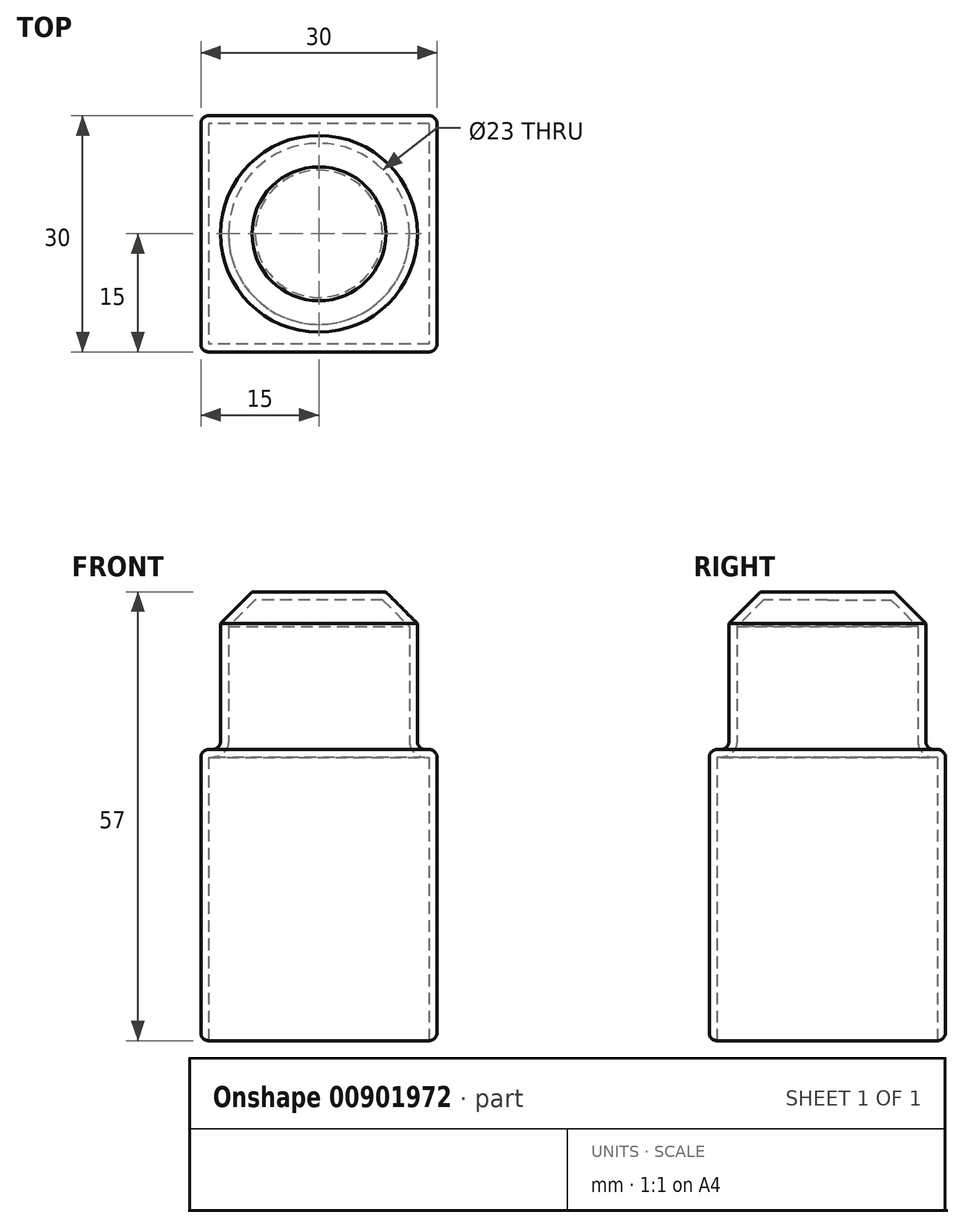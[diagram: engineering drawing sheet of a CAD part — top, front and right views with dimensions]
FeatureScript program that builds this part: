
annotation { "Feature Type Name" : "Feature", "Feature Type Description" : "" }
export const myFeature = defineFeature(function(context is Context, id is Id, definition is map)
    precondition{}
    {
        {
            var Q0;
            Q0=qCreatedBy(makeId("Top.planeOp"),FACE);
            var sketch = newSketch(context, id + "F0", { "sketchPlane" : qUnion([Q0])});
            skLineSegment(sketch, "E0.bottom", {"start": v(15, 15) * mm, "end": v(-15, 15) * mm});
            skLineSegment(sketch, "E0.top", {"start": v(15, -15) * mm, "end": v(-15, -15) * mm});
            skLineSegment(sketch, "E0.left", {"start": v(15, 15) * mm, "end": v(15, -15) * mm});
            skLineSegment(sketch, "E0.right", {"start": v(-15, 15) * mm, "end": v(-15, -15) * mm});
            skPoint(sketch, "E0.middle", {"position": v(0, 0) * mm});
            skSolve(sketch);
        }
        {
            var Q0;
            Q0 = qSketchRegion(id + "F0", true);
            extrude(context, id + "F1", {"entities" : qUnion([Q0]), "depth" : 37 * mm, "offsetDistance" : 25 * mm});
        }
        {
            var Q0;
            Q0=makeQuery(id+"F1.opExtrude","CAP_FACE",FACE,{"disambiguationData":[OSD([sQuery(id+"F0.wireOp",EDGE,"E0.bottom"),sQuery(id+"F0.wireOp",EDGE,"E0.top"),sQuery(id+"F0.wireOp",EDGE,"E0.left"),sQuery(id+"F0.wireOp",EDGE,"E0.right")])],"isStart":false});
            var sketch = newSketch(context, id + "F2", { "sketchPlane" : qUnion([Q0])});
            skCircle(sketch, "E1", {"center": v(0, 0) * mm, "radius": 12.5 * mm});
            skSolve(sketch);
        }
        {
            var Q0;
            Q0 = qSketchRegion(id + "F2", true);
            extrude(context, id + "F3", {"entities" : qUnion([Q0]), "operationType" : NewBodyOperationType.ADD, "depth" : 20 * mm, "offsetDistance" : 25 * mm});
        }
        {
            var Q0;
            Q0=makeQuery(id+"F3.opExtrude","CAP_EDGE",EDGE,{"disambiguationData":[OSD([sQuery(id+"F2.wireOp",EDGE,"E1")])],"isStart":false});
            chamfer(context, id + "F4", {"entities" : qUnion([Q0]), "width" : 4 * mm, "tangentPropagation" : true});
        }
        {
            var Q0;
            Q0=makeQuery(id+"F1.opExtrude","SWEPT_FACE",FACE,{"disambiguationData":[OSD([sQuery(id+"F0.wireOp",EDGE,"E0.top")])]});
            var Q1;
            Q1=makeQuery(id+"F1.opExtrude","SWEPT_FACE",FACE,{"disambiguationData":[OSD([sQuery(id+"F0.wireOp",EDGE,"E0.left")])]});
            var Q2;
            Q2=makeQuery(id+"F1.opExtrude","SWEPT_FACE",FACE,{"disambiguationData":[OSD([sQuery(id+"F0.wireOp",EDGE,"E0.right")])]});
            var Q3;
            Q3=makeQuery(id+"F1.opExtrude","SWEPT_FACE",FACE,{"disambiguationData":[OSD([sQuery(id+"F0.wireOp",EDGE,"E0.bottom")])]});
            var Q4;
            Q4=makeQuery(id+"F1.opExtrude","CAP_FACE",FACE,{"disambiguationData":[OSD([sQuery(id+"F0.wireOp",EDGE,"E0.bottom"),sQuery(id+"F0.wireOp",EDGE,"E0.top"),sQuery(id+"F0.wireOp",EDGE,"E0.left"),sQuery(id+"F0.wireOp",EDGE,"E0.right")])],"isStart":false});
            fillet(context, id + "F5", {"entities" : qUnion([Q0, Q1, Q2, Q3, Q4]), "radius" : 1 * mm, "tangentPropagation" : true, "allowEdgeOverflow" : false});
        }
        {
            var Q0;
            Q0=makeQuery(id+"F1.opExtrude","CAP_FACE",FACE,{"disambiguationData":[OSD([sQuery(id+"F0.wireOp",EDGE,"E0.bottom"),sQuery(id+"F0.wireOp",EDGE,"E0.top"),sQuery(id+"F0.wireOp",EDGE,"E0.left"),sQuery(id+"F0.wireOp",EDGE,"E0.right")])],"isStart":true});
            shell(context, id + "F6", {"entities" : qUnion([Q0]), "thickness" : 1 * mm});
        }
    });
